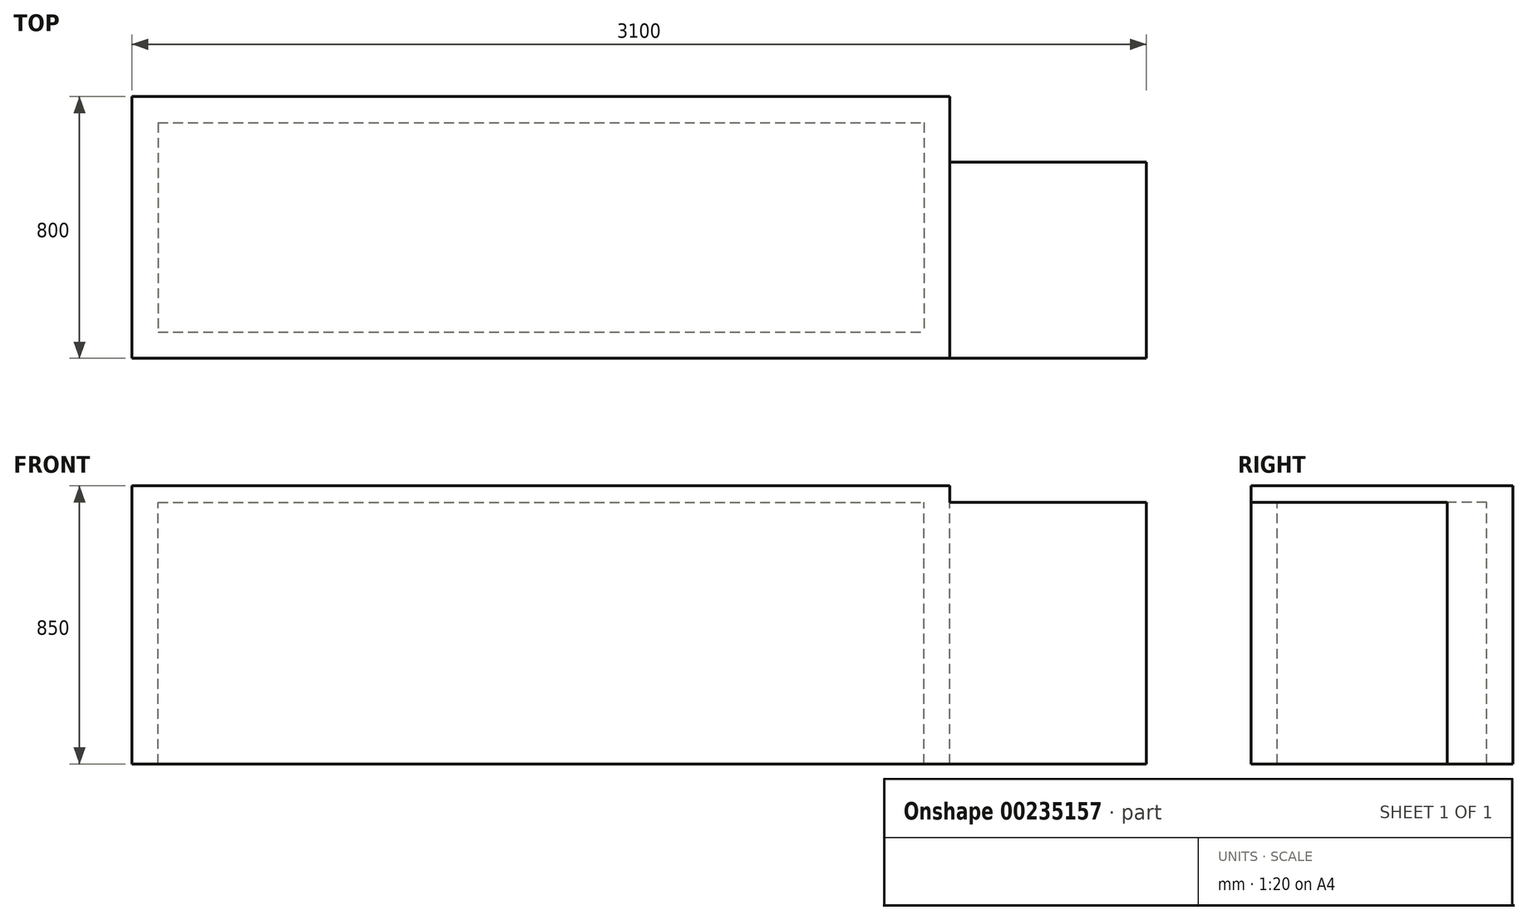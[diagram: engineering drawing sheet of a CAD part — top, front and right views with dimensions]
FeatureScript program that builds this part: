
annotation { "Feature Type Name" : "Feature", "Feature Type Description" : "" }
export const myFeature = defineFeature(function(context is Context, id is Id, definition is map)
    precondition{}
    {
        {
            var Q0;
            Q0=qCreatedBy(makeId("Top.planeOp"),FACE);
            var sketch = newSketch(context, id + "F0", { "sketchPlane" : qUnion([Q0])});
            skLineSegment(sketch, "E0.bottom", {"start": v(-1250, 400) * mm, "end": v(1250, 400) * mm});
            skLineSegment(sketch, "E0.top", {"start": v(-1250, -400) * mm, "end": v(1250, -400) * mm});
            skLineSegment(sketch, "E0.left", {"start": v(-1250, 400) * mm, "end": v(-1250, -400) * mm});
            skLineSegment(sketch, "E0.right", {"start": v(1250, 400) * mm, "end": v(1250, -400) * mm});
            skPoint(sketch, "E0.middle", {"position": v(0, 0) * mm});
            skLineSegment(sketch, "E1", {"start": v(-450, 400) * mm, "end": v(-450, -400) * mm});
            skLineSegment(sketch, "E2.bottom", {"start": v(-1150, -100) * mm, "end": v(-550, -100) * mm});
            skLineSegment(sketch, "E2.top", {"start": v(-1150, 250) * mm, "end": v(-550, 250) * mm});
            skLineSegment(sketch, "E2.left", {"start": v(-1150, -100) * mm, "end": v(-1150, 250) * mm});
            skLineSegment(sketch, "E2.right", {"start": v(-550, -100) * mm, "end": v(-550, 250) * mm});
            skPoint(sketch, "E2.middle", {"position": v(-850, 75) * mm});
            skLineSegment(sketch, "E3", {"start": v(450, 400) * mm, "end": v(450, -400) * mm});
            skCircle(sketch, "E4", {"center": v(686.44, 127.78) * mm, "radius": 81.89 * mm});
            skCircle(sketch, "E5", {"center": v(983.98, 136.66) * mm, "radius": 75.63 * mm});
            skLineSegment(sketch, "E6.bottom", {"start": v(1250, -400) * mm, "end": v(1850, -400) * mm});
            skLineSegment(sketch, "E6.top", {"start": v(1250, 200) * mm, "end": v(1850, 200) * mm});
            skLineSegment(sketch, "E6.left", {"start": v(1250, -400) * mm, "end": v(1250, 200) * mm});
            skLineSegment(sketch, "E6.right", {"start": v(1850, -400) * mm, "end": v(1850, 200) * mm});
            skLineSegment(sketch, "E7.bottom", {"start": v(-1170, 320) * mm, "end": v(1170, 320) * mm});
            skLineSegment(sketch, "E7.top", {"start": v(-1170, -320) * mm, "end": v(1170, -320) * mm});
            skLineSegment(sketch, "E7.left", {"start": v(-1170, 320) * mm, "end": v(-1170, -320) * mm});
            skLineSegment(sketch, "E7.right", {"start": v(1170, 320) * mm, "end": v(1170, -320) * mm});
            skSolve(sketch);
        }
        {
            var Q0;
            {var subQ0=sQuery(id+"F0.wireOp",EDGE,"E0.left");Q0=makeQuery(id+"F0.imprint","IMPRINT",FACE,{"disambiguationData":[TD([[makeQuery(id+"F0.imprint","IMPRINT",EDGE,{"derivedFrom":subQ0}),1.0]])]});}
            var Q1;
            {var subQ0=sQuery(id+"F0.wireOp",EDGE,"E1");var subQ1=sQuery(id+"F0.wireOp",EDGE,"E0.bottom");var subQ2=makeQuery(id+"F0.imprint","INTERSECT",VERTEX,{"derivedFrom":[subQ1,subQ0]});Q1=makeQuery(id+"F0.imprint","IMPRINT",FACE,{"disambiguationData":[TD([[makeQuery(id+"F0.imprint","IMPRINT",EDGE,{"disambiguationData":[TD([[subQ2,-1.0]])],"derivedFrom":subQ1}),-1.0]])]});}
            var Q2;
            {var subQ9=sQuery(id+"F0.wireOp",EDGE,"E0.right");Q2=makeQuery(id+"F0.imprint","IMPRINT",FACE,{"disambiguationData":[TD([[makeQuery(id+"F0.imprint","IMPRINT",EDGE,{"derivedFrom":subQ9}),-1.0]])]});}
            var Q3;
            {var subQ0=sQuery(id+"F0.wireOp",EDGE,"E1");var subQ1=sQuery(id+"F0.wireOp",EDGE,"E0.top");var subQ2=makeQuery(id+"F0.imprint","INTERSECT",VERTEX,{"derivedFrom":[subQ1,subQ0]});Q3=makeQuery(id+"F0.imprint","IMPRINT",FACE,{"disambiguationData":[TD([[makeQuery(id+"F0.imprint","IMPRINT",EDGE,{"disambiguationData":[TD([[subQ2,-1.0]])],"derivedFrom":subQ1}),1.0]])]});}
            extrude(context, id + "F1", {"entities" : qUnion([Q0, Q1, Q2, Q3]), "oppositeDirection" : true, "depth" : 800 * mm, "offsetDistance" : 25 * mm});
        }
        {
            var Q0;
            Q0=makeQuery(id+"F1.opExtrude","SWEPT_FACE",FACE,{"disambiguationData":[OSD([sQuery(id+"F0.wireOp",EDGE,"E0.top")])]});
            var sketch = newSketch(context, id + "F2", { "sketchPlane" : qUnion([Q0])});
            skLineSegment(sketch, "E8.bottom", {"start": v(-1250, 0) * mm, "end": v(1250, 0) * mm});
            skLineSegment(sketch, "E8.top", {"start": v(-1250, 50) * mm, "end": v(1250, 50) * mm});
            skLineSegment(sketch, "E8.left", {"start": v(-1250, 0) * mm, "end": v(-1250, 50) * mm});
            skLineSegment(sketch, "E8.right", {"start": v(1250, 0) * mm, "end": v(1250, 50) * mm});
            skSolve(sketch);
        }
        {
            var Q0;
            Q0=makeQuery(id+"F2.imprint","IMPRINT",FACE,{"disambiguationData":[TD([[makeQuery(id+"F2.imprint","IMPRINT",EDGE,{"derivedFrom":sQuery(id+"F2.wireOp",EDGE,"E8.bottom")}),1.0]])]});
            extrude(context, id + "F3", {"entities" : qUnion([Q0]), "oppositeDirection" : true, "depth" : 800 * mm, "offsetDistance" : 25 * mm});
        }
        {
            var Q0;
            Q0=makeQuery(id+"F0.imprint","IMPRINT",FACE,{"disambiguationData":[TD([[makeQuery(id+"F0.imprint","IMPRINT",EDGE,{"derivedFrom":sQuery(id+"F0.wireOp",EDGE,"E6.bottom")}),1.0]])]});
            extrude(context, id + "F4", {"entities" : qUnion([Q0]), "operationType" : NewBodyOperationType.ADD, "oppositeDirection" : true, "depth" : 800 * mm, "offsetDistance" : 25 * mm});
        }
    });
